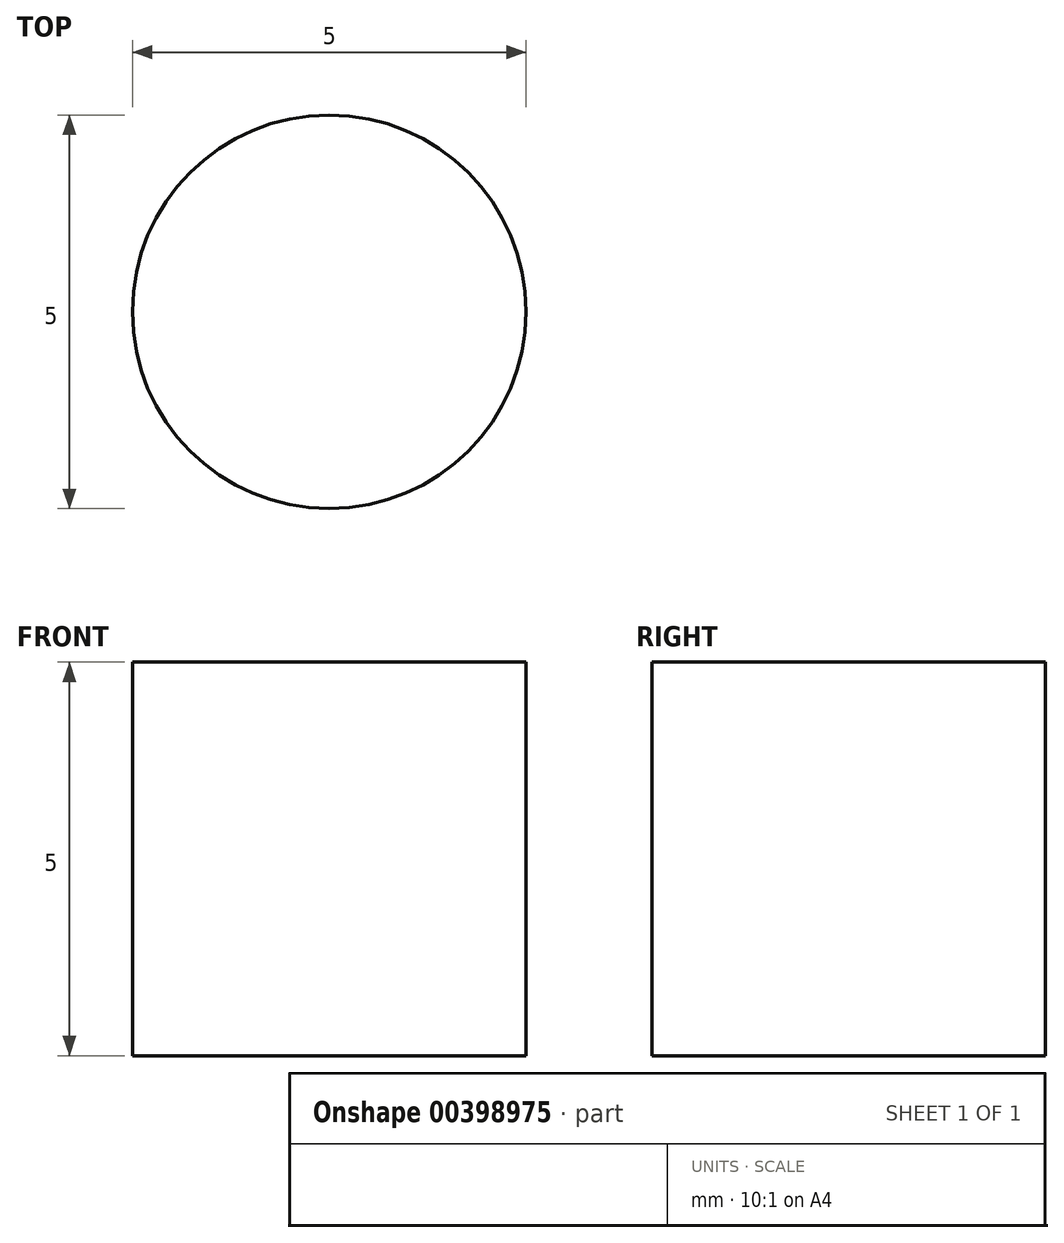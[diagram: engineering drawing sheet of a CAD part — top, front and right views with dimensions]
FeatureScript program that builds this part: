
annotation { "Feature Type Name" : "Feature", "Feature Type Description" : "" }
export const myFeature = defineFeature(function(context is Context, id is Id, definition is map)
    precondition{}
    {
        {
            var Q0;
            Q0=qCreatedBy(makeId("Top.planeOp"),FACE);
            var sketch = newSketch(context, id + "F0", { "sketchPlane" : qUnion([Q0])});
            skCircle(sketch, "E0", {"center": v(0, 0) * mm, "radius": 2.5 * mm});
            skSolve(sketch);
        }
        {
            var Q0;
            Q0=makeQuery(id+"F0.imprint","IMPRINT",FACE,{"disambiguationData":[TD([[makeQuery(id+"F0.imprint","IMPRINT",EDGE,{"derivedFrom":sQuery(id+"F0.wireOp",EDGE,"E0")}),1.0]])]});
            extrude(context, id + "F1", {"entities" : qUnion([Q0]), "depth" : 5 * mm});
        }
    });
